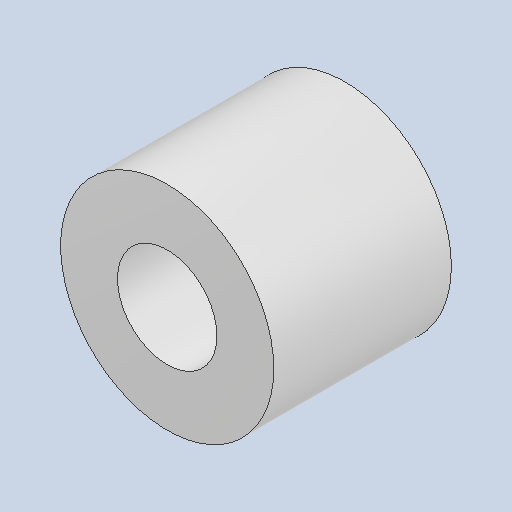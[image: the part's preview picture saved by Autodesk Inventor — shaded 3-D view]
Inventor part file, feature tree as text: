
AUTODESK INVENTOR PART (.ipt)
format: ipt  version: 2023 (Build 270158030, 158C)  size: 116,224 bytes
history: native  units: mm
features: other x1, extrude x1, sketch x1
ambient origin geometry x8: Origin, YZ Plane, XZ Plane, XY Plane, X Axis, Y Axis, Z Axis, Center Point
bodies: Body1 (feature_tree)
feature tree (3):
  other  "ソリッド1"
  extrude  "押し出し1"  Depth=6.0mm
  sketch  "スケッチ1"
